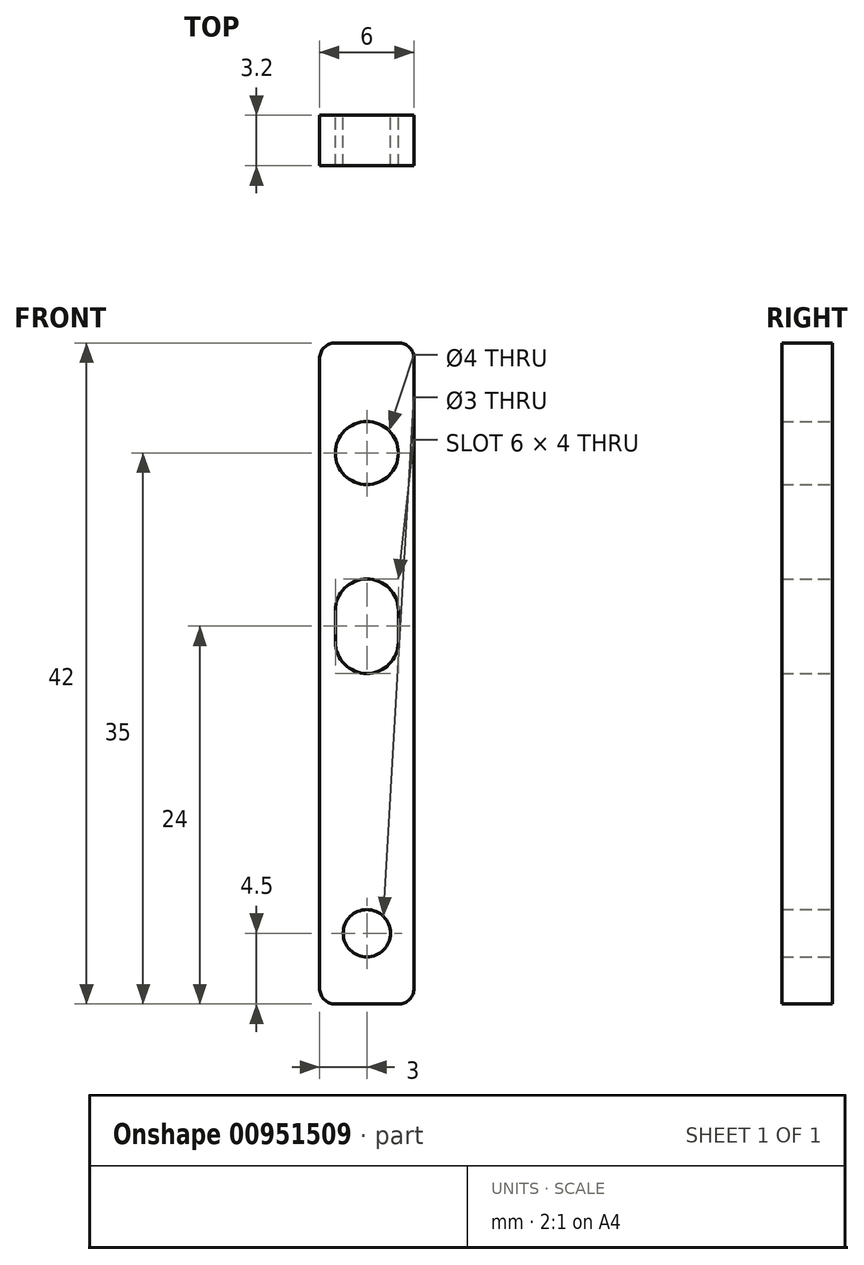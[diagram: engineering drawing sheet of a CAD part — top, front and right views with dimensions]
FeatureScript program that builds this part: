
annotation { "Feature Type Name" : "Feature", "Feature Type Description" : "" }
export const myFeature = defineFeature(function(context is Context, id is Id, definition is map)
    precondition{}
    {
        {
            var Q0;
            Q0=qCreatedBy(makeId("Front.planeOp"),FACE);
            var sketch = newSketch(context, id + "F0", { "sketchPlane" : qUnion([Q0])});
            skPoint(sketch, "E0.middle", {"position": v(0, 0) * mm});
            skCircle(sketch, "E1", {"center": v(0, 0) * mm, "radius": 2 * mm});
            skCircle(sketch, "E2", {"center": v(0, -10) * mm, "radius": 2 * mm});
            skCircle(sketch, "E3", {"center": v(0, -12) * mm, "radius": 2 * mm});
            skLineSegment(sketch, "E4", {"start": v(3, 6) * mm, "end": v(3, -34) * mm});
            skLineSegment(sketch, "E5", {"start": v(2, -35) * mm, "end": v(-2, -35) * mm});
            skLineSegment(sketch, "E6", {"start": v(-3, -34) * mm, "end": v(-3, 6) * mm});
            skLineSegment(sketch, "E7", {"start": v(-2, 7) * mm, "end": v(2, 7) * mm});
            skCircle(sketch, "E8", {"center": v(0, -30.5) * mm, "radius": 1.5 * mm});
            skLineSegment(sketch, "E9", {"start": v(-2, -10) * mm, "end": v(-2, -12) * mm});
            skLineSegment(sketch, "E10", {"start": v(2, -10) * mm, "end": v(2, -12) * mm});
            skPoint(sketch, "E11.visualSharp", {"position": v(3, 7) * mm});
            skArc(sketch, "E11.filletArc", {"start": v(3, 6) * mm, "mid": v(2.7, 6.7) * mm, "end": v(2, 7) * mm});
            skPoint(sketch, "E12.visualSharp", {"position": v(-3, 7) * mm});
            skArc(sketch, "E12.filletArc", {"start": v(-2, 7) * mm, "mid": v(-2.7, 6.7) * mm, "end": v(-3, 6) * mm});
            skPoint(sketch, "E13.visualSharp", {"position": v(-3, -35) * mm});
            skArc(sketch, "E13.filletArc", {"start": v(-3, -34) * mm, "mid": v(-2.7, -34.7) * mm, "end": v(-2, -35) * mm});
            skPoint(sketch, "E14.visualSharp", {"position": v(3, -35) * mm});
            skArc(sketch, "E14.filletArc", {"start": v(2, -35) * mm, "mid": v(2.7, -34.7) * mm, "end": v(3, -34) * mm});
            skSolve(sketch);
        }
        {
            var Q0;
            Q0 = qSketchRegion(id + "F0", true);
            extrude(context, id + "F1", {"entities" : qUnion([Q0]), "depth" : 3.2 * mm, "offsetDistance" : 25 * mm});
        }
    });
